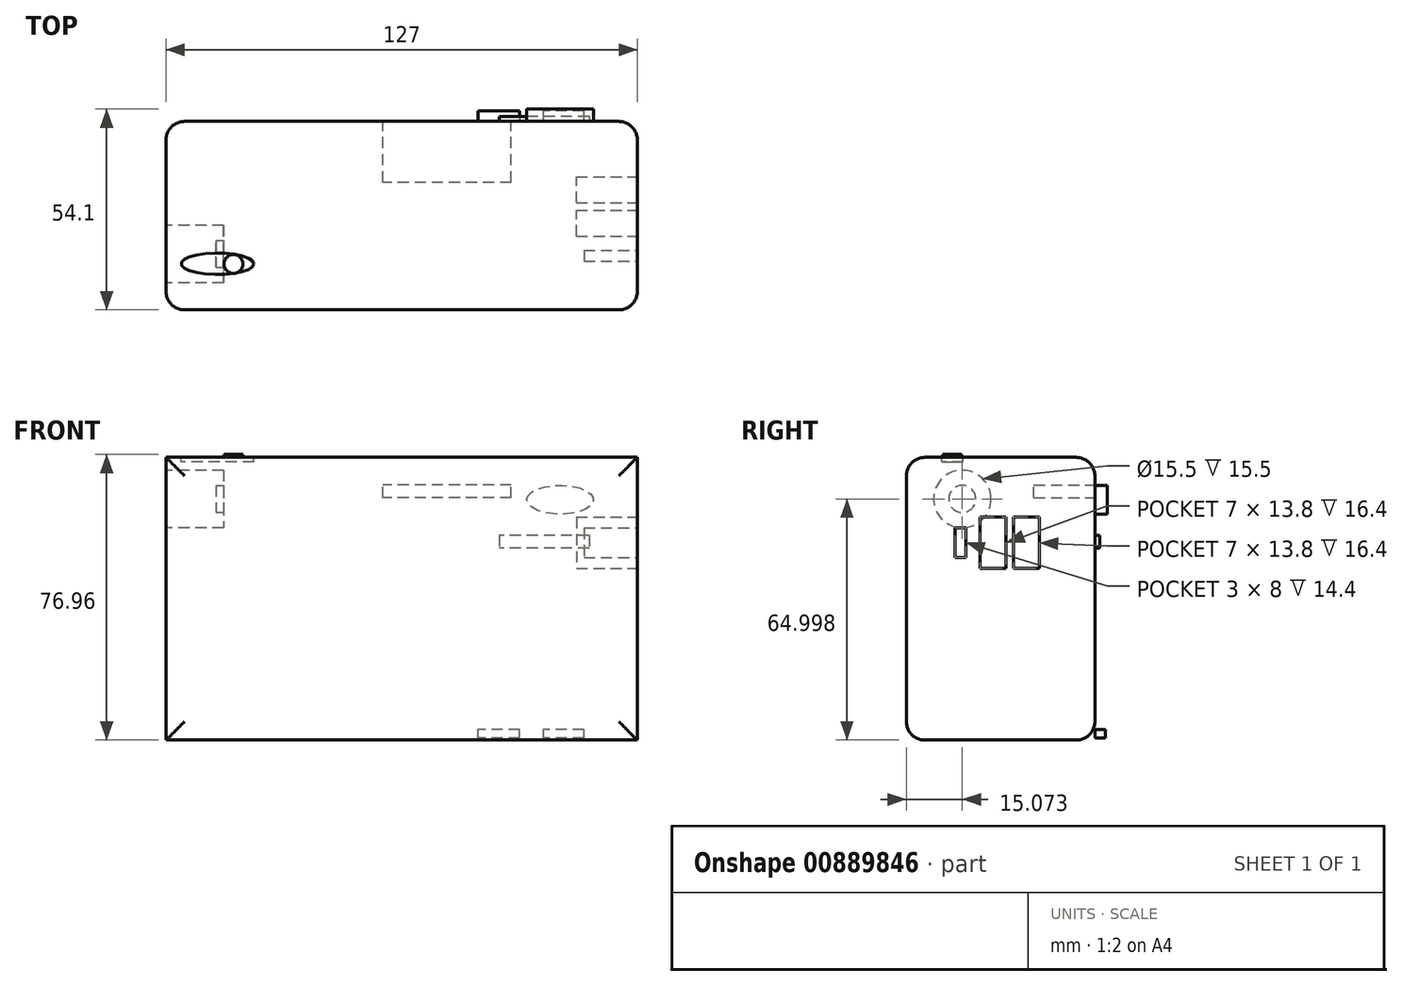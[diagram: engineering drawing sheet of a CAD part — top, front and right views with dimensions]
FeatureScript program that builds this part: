
annotation { "Feature Type Name" : "Feature", "Feature Type Description" : "" }
export const myFeature = defineFeature(function(context is Context, id is Id, definition is map)
    precondition{}
    {
        {
            var Q0;
            Q0=qCreatedBy(makeId("Front.planeOp"),FACE);
            var sketch = newSketch(context, id + "F0", { "sketchPlane" : qUnion([Q0])});
            skLineSegment(sketch, "E0.bottom", {"start": v(63.5, -38.1) * mm, "end": v(-63.5, -38.1) * mm});
            skLineSegment(sketch, "E0.top", {"start": v(63.5, 38.1) * mm, "end": v(-63.5, 38.1) * mm});
            skLineSegment(sketch, "E0.left", {"start": v(63.5, -38.1) * mm, "end": v(63.5, 38.1) * mm});
            skLineSegment(sketch, "E0.right", {"start": v(-63.5, -38.1) * mm, "end": v(-63.5, 38.1) * mm});
            skPoint(sketch, "E0.middle", {"position": v(0, 0) * mm});
            skSolve(sketch);
        }
        {
            var Q0;
            Q0 = qSketchRegion(id + "F0", true);
            extrude(context, id + "F1", {"entities" : qUnion([Q0]), "depth" : 50.8 * mm, "offsetDistance" : 25.4 * mm});
        }
        {
            var Q0;
            Q0=makeQuery(id+"F1.opExtrude","CAP_EDGE",EDGE,{"disambiguationData":[OSD([sQuery(id+"F0.wireOp",EDGE,"E0.bottom")])],"isStart":false});
            var Q1;
            Q1=makeQuery(id+"F1.opExtrude","CAP_EDGE",EDGE,{"disambiguationData":[OSD([sQuery(id+"F0.wireOp",EDGE,"E0.bottom")])],"isStart":true});
            var Q2;
            Q2=makeQuery(id+"F1.opExtrude","CAP_FACE",FACE,{"disambiguationData":[OSD([sQuery(id+"F0.wireOp",EDGE,"E0.bottom"),sQuery(id+"F0.wireOp",EDGE,"E0.top"),sQuery(id+"F0.wireOp",EDGE,"E0.left"),sQuery(id+"F0.wireOp",EDGE,"E0.right")])],"isStart":true});
            var Q3;
            Q3=makeQuery(id+"F1.opExtrude","CAP_EDGE",EDGE,{"disambiguationData":[OSD([sQuery(id+"F0.wireOp",EDGE,"E0.top")])],"isStart":false});
            var Q4;
            Q4=makeQuery(id+"F1.opExtrude","CAP_EDGE",EDGE,{"disambiguationData":[OSD([sQuery(id+"F0.wireOp",EDGE,"E0.left")])],"isStart":false});
            var Q5;
            Q5=makeQuery(id+"F1.opExtrude","CAP_FACE",FACE,{"disambiguationData":[OSD([sQuery(id+"F0.wireOp",EDGE,"E0.bottom"),sQuery(id+"F0.wireOp",EDGE,"E0.top"),sQuery(id+"F0.wireOp",EDGE,"E0.left"),sQuery(id+"F0.wireOp",EDGE,"E0.right")])],"isStart":false});
            fillet(context, id + "F2", {"entities" : qUnion([Q0, Q1, Q2, Q3, Q4, Q5]), "radius" : 5 * mm, "tangentPropagation" : true, "allowEdgeOverflow" : false});
        }
        {
            var Q0;
            Q0=makeQuery(id+"F1.opExtrude","SWEPT_FACE",FACE,{"disambiguationData":[OSD([sQuery(id+"F0.wireOp",EDGE,"E0.left")])]});
            var sketch = newSketch(context, id + "F3", { "sketchPlane" : qUnion([Q0])});
            skLineSegment(sketch, "E1.bottom", {"start": v(-30.94, 22) * mm, "end": v(-23.94, 22) * mm});
            skLineSegment(sketch, "E1.top", {"start": v(-30.94, 8.2) * mm, "end": v(-23.94, 8.2) * mm});
            skLineSegment(sketch, "E1.left", {"start": v(-30.94, 22) * mm, "end": v(-30.94, 8.2) * mm});
            skLineSegment(sketch, "E1.right", {"start": v(-23.94, 22) * mm, "end": v(-23.94, 8.2) * mm});
            skSolve(sketch);
        }
        {
            var Q0;
            Q0=makeQuery(id+"F3.imprint","IMPRINT",FACE,{"disambiguationData":[TD([[makeQuery(id+"F3.imprint","IMPRINT",EDGE,{"derivedFrom":sQuery(id+"F3.wireOp",EDGE,"E1.bottom")}),-1.0]])]});
            extrude(context, id + "F4", {"entities" : qUnion([Q0]), "operationType" : NewBodyOperationType.REMOVE, "oppositeDirection" : true, "depth" : 16.4 * mm, "offsetDistance" : 25.4 * mm});
        }
        {
            var Q0;
            Q0=makeQuery(id+"F1.opExtrude","SWEPT_FACE",FACE,{"disambiguationData":[OSD([sQuery(id+"F0.wireOp",EDGE,"E0.left")])]});
            var sketch = newSketch(context, id + "F5", { "sketchPlane" : qUnion([Q0])});
            skLineSegment(sketch, "E2.bottom", {"start": v(-21.93, 22) * mm, "end": v(-14.93, 22) * mm});
            skLineSegment(sketch, "E2.top", {"start": v(-21.93, 8.2) * mm, "end": v(-14.93, 8.2) * mm});
            skLineSegment(sketch, "E2.left", {"start": v(-21.93, 22) * mm, "end": v(-21.93, 8.2) * mm});
            skLineSegment(sketch, "E2.right", {"start": v(-14.93, 22) * mm, "end": v(-14.93, 8.2) * mm});
            skSolve(sketch);
        }
        {
            var Q0;
            Q0=makeQuery(id+"F5.imprint","IMPRINT",FACE,{"disambiguationData":[TD([[makeQuery(id+"F5.imprint","IMPRINT",EDGE,{"derivedFrom":sQuery(id+"F5.wireOp",EDGE,"E2.bottom")}),-1.0]])]});
            extrude(context, id + "F6", {"entities" : qUnion([Q0]), "operationType" : NewBodyOperationType.REMOVE, "oppositeDirection" : true, "depth" : 16.4 * mm, "offsetDistance" : 25.4 * mm});
        }
        {
            var Q0;
            Q0=makeQuery(id+"F1.opExtrude","SWEPT_FACE",FACE,{"disambiguationData":[OSD([sQuery(id+"F0.wireOp",EDGE,"E0.left")])]});
            var sketch = newSketch(context, id + "F7", { "sketchPlane" : qUnion([Q0])});
            skLineSegment(sketch, "E3.bottom", {"start": v(-34.73, 19.1) * mm, "end": v(-37.73, 19.1) * mm});
            skLineSegment(sketch, "E3.top", {"start": v(-34.73, 11.1) * mm, "end": v(-37.73, 11.1) * mm});
            skLineSegment(sketch, "E3.left", {"start": v(-34.73, 19.1) * mm, "end": v(-34.73, 11.1) * mm});
            skLineSegment(sketch, "E3.right", {"start": v(-37.73, 19.1) * mm, "end": v(-37.73, 11.1) * mm});
            skSolve(sketch);
        }
        {
            var Q0;
            Q0 = qSketchRegion(id + "F7", true);
            extrude(context, id + "F8", {"entities" : qUnion([Q0]), "operationType" : NewBodyOperationType.REMOVE, "oppositeDirection" : true, "depth" : 14.4 * mm, "offsetDistance" : 25.4 * mm});
        }
        {
            var Q0;
            Q0=makeQuery(id+"F1.opExtrude","SWEPT_FACE",FACE,{"disambiguationData":[OSD([sQuery(id+"F0.wireOp",EDGE,"E0.right")])]});
            var sketch = newSketch(context, id + "F9", { "sketchPlane" : qUnion([Q0])});
            skCircle(sketch, "E4", {"center": v(35.73, 26.9) * mm, "radius": 7.75 * mm});
            skSolve(sketch);
        }
        {
            var Q0;
            Q0 = qSketchRegion(id + "F9", true);
            var Q1;
            Q1=makeQuery(id+"F9.imprint","IMPRINT",FACE,{"disambiguationData":[TD([[makeQuery(id+"F9.imprint","IMPRINT",EDGE,{"derivedFrom":sQuery(id+"F9.wireOp",EDGE,"E4")}),1.0]])]});
            extrude(context, id + "F10", {"entities" : qUnion([Q0, Q1]), "operationType" : NewBodyOperationType.REMOVE, "oppositeDirection" : true, "depth" : 15.5 * mm, "offsetDistance" : 25.4 * mm});
        }
        {
            var Q0;
            Q0=makeQuery(id+"F10.boolean.opBoolean","COPY",FACE,{"derivedFrom":makeQuery(id+"F10.opExtrude","CAP_FACE",FACE,{"disambiguationData":[OSD([sQuery(id+"F9.wireOp",EDGE,"E4")])],"isStart":false})});
            var sketch = newSketch(context, id + "F11", { "sketchPlane" : qUnion([Q0])});
            skCircle(sketch, "E5", {"center": v(35.73, 26.9) * mm, "radius": 3.65 * mm});
            skSolve(sketch);
        }
        {
            var Q0;
            Q0 = qSketchRegion(id + "F11", true);
            extrude(context, id + "F12", {"entities" : qUnion([Q0]), "operationType" : NewBodyOperationType.ADD, "depth" : 2.03 * mm, "offsetDistance" : 25.4 * mm});
        }
        {
            var Q0;
            Q0=makeQuery(id+"F1.opExtrude","SWEPT_FACE",FACE,{"disambiguationData":[OSD([sQuery(id+"F0.wireOp",EDGE,"E0.top")])]});
            var sketch = newSketch(context, id + "F13", { "sketchPlane" : qUnion([Q0])});
            skEllipse(sketch, "E6", {"center": v(-49.63, -38.38) * mm, "majorRadius": 9.78 * mm, "minorRadius": 2.9 * mm, "majorAxis": v(1, 0)});
            skSolve(sketch);
        }
        {
            var Q0;
            Q0 = qSketchRegion(id + "F13", true);
            extrude(context, id + "F14", {"entities" : qUnion([Q0]), "operationType" : NewBodyOperationType.REMOVE, "oppositeDirection" : true, "depth" : 1.27 * mm, "offsetDistance" : 25.4 * mm});
        }
        {
            var Q0;
            Q0=makeQuery(id+"F1.opExtrude","SWEPT_FACE",FACE,{"disambiguationData":[OSD([sQuery(id+"F0.wireOp",EDGE,"E0.top")])]});
            var sketch = newSketch(context, id + "F15", { "sketchPlane" : qUnion([Q0])});
            skCircle(sketch, "E7", {"center": v(-45.33, -38.42) * mm, "radius": 2.55 * mm});
            skSolve(sketch);
        }
        {
            var Q0;
            Q0 = qSketchRegion(id + "F15", true);
            extrude(context, id + "F16", {"entities" : qUnion([Q0]), "depth" : 0.76 * mm, "offsetDistance" : 25.4 * mm});
        }
        {
            var Q0;
            Q0=makeQuery(id+"F1.opExtrude","CAP_FACE",FACE,{"disambiguationData":[OSD([sQuery(id+"F0.wireOp",EDGE,"E0.bottom"),sQuery(id+"F0.wireOp",EDGE,"E0.top"),sQuery(id+"F0.wireOp",EDGE,"E0.left"),sQuery(id+"F0.wireOp",EDGE,"E0.right")])],"isStart":true});
            var sketch = newSketch(context, id + "F17", { "sketchPlane" : qUnion([Q0])});
            skEllipse(sketch, "E8", {"center": v(-42.69, 26.68) * mm, "majorRadius": 8.97 * mm, "minorRadius": 3.89 * mm, "majorAxis": v(1, 0)});
            skSolve(sketch);
        }
        {
            var Q0;
            Q0 = qSketchRegion(id + "F17", true);
            extrude(context, id + "F18", {"entities" : qUnion([Q0]), "operationType" : NewBodyOperationType.ADD, "depth" : 3.3 * mm, "offsetDistance" : 25.4 * mm});
        }
        {
            var Q0;
            Q0=makeQuery(id+"F1.opExtrude","CAP_FACE",FACE,{"disambiguationData":[OSD([sQuery(id+"F0.wireOp",EDGE,"E0.bottom"),sQuery(id+"F0.wireOp",EDGE,"E0.top"),sQuery(id+"F0.wireOp",EDGE,"E0.left"),sQuery(id+"F0.wireOp",EDGE,"E0.right")])],"isStart":true});
            var sketch = newSketch(context, id + "F19", { "sketchPlane" : qUnion([Q0])});
            skLineSegment(sketch, "E9.bottom", {"start": v(-29.5, 27.2) * mm, "end": v(5.04, 27.2) * mm});
            skLineSegment(sketch, "E9.top", {"start": v(-29.5, 30.65) * mm, "end": v(5.04, 30.65) * mm});
            skLineSegment(sketch, "E9.left", {"start": v(-29.5, 27.2) * mm, "end": v(-29.5, 30.65) * mm});
            skLineSegment(sketch, "E9.right", {"start": v(5.04, 27.2) * mm, "end": v(5.04, 30.65) * mm});
            skSolve(sketch);
        }
        {
            var Q0;
            Q0 = qSketchRegion(id + "F19", true);
            extrude(context, id + "F20", {"entities" : qUnion([Q0]), "operationType" : NewBodyOperationType.REMOVE, "oppositeDirection" : true, "depth" : 16.4 * mm, "offsetDistance" : 25.4 * mm});
        }
        {
            var Q0;
            Q0=makeQuery(id+"F1.opExtrude","CAP_FACE",FACE,{"disambiguationData":[OSD([sQuery(id+"F0.wireOp",EDGE,"E0.bottom"),sQuery(id+"F0.wireOp",EDGE,"E0.top"),sQuery(id+"F0.wireOp",EDGE,"E0.left"),sQuery(id+"F0.wireOp",EDGE,"E0.right")])],"isStart":true});
            var sketch = newSketch(context, id + "F21", { "sketchPlane" : qUnion([Q0])});
            skLineSegment(sketch, "E10.bottom", {"start": v(-49.07, -35.26) * mm, "end": v(-38.13, -35.26) * mm});
            skLineSegment(sketch, "E10.top", {"start": v(-49.07, -37.56) * mm, "end": v(-38.13, -37.56) * mm});
            skLineSegment(sketch, "E10.left", {"start": v(-49.07, -35.26) * mm, "end": v(-49.07, -37.56) * mm});
            skLineSegment(sketch, "E10.right", {"start": v(-38.13, -35.26) * mm, "end": v(-38.13, -37.56) * mm});
            skLineSegment(sketch, "E11.bottom", {"start": v(-31.8, -37.56) * mm, "end": v(-20.58, -37.56) * mm});
            skLineSegment(sketch, "E11.top", {"start": v(-31.8, -35.26) * mm, "end": v(-20.58, -35.26) * mm});
            skLineSegment(sketch, "E11.left", {"start": v(-31.8, -37.56) * mm, "end": v(-31.8, -35.26) * mm});
            skLineSegment(sketch, "E11.right", {"start": v(-20.58, -37.56) * mm, "end": v(-20.58, -35.26) * mm});
            skSolve(sketch);
        }
        {
            var Q0;
            Q0 = qSketchRegion(id + "F21", true);
            extrude(context, id + "F22", {"entities" : qUnion([Q0]), "depth" : 2.8 * mm, "offsetDistance" : 25.4 * mm});
        }
        {
            var Q0;
            Q0=makeQuery(id+"F1.opExtrude","CAP_FACE",FACE,{"disambiguationData":[OSD([sQuery(id+"F0.wireOp",EDGE,"E0.bottom"),sQuery(id+"F0.wireOp",EDGE,"E0.top"),sQuery(id+"F0.wireOp",EDGE,"E0.left"),sQuery(id+"F0.wireOp",EDGE,"E0.right")])],"isStart":true});
            var sketch = newSketch(context, id + "F23", { "sketchPlane" : qUnion([Q0])});
            skLineSegment(sketch, "E12.bottom", {"start": v(-50.5, 17.12) * mm, "end": v(-26.33, 17.12) * mm});
            skLineSegment(sketch, "E12.top", {"start": v(-50.5, 13.67) * mm, "end": v(-26.33, 13.67) * mm});
            skLineSegment(sketch, "E12.left", {"start": v(-50.5, 17.12) * mm, "end": v(-50.5, 13.67) * mm});
            skLineSegment(sketch, "E12.right", {"start": v(-26.33, 17.12) * mm, "end": v(-26.33, 13.67) * mm});
            skSolve(sketch);
        }
        {
            var Q0;
            Q0 = qSketchRegion(id + "F23", true);
            extrude(context, id + "F24", {"entities" : qUnion([Q0]), "operationType" : NewBodyOperationType.ADD, "depth" : 1.27 * mm, "offsetDistance" : 25.4 * mm});
        }
    });
